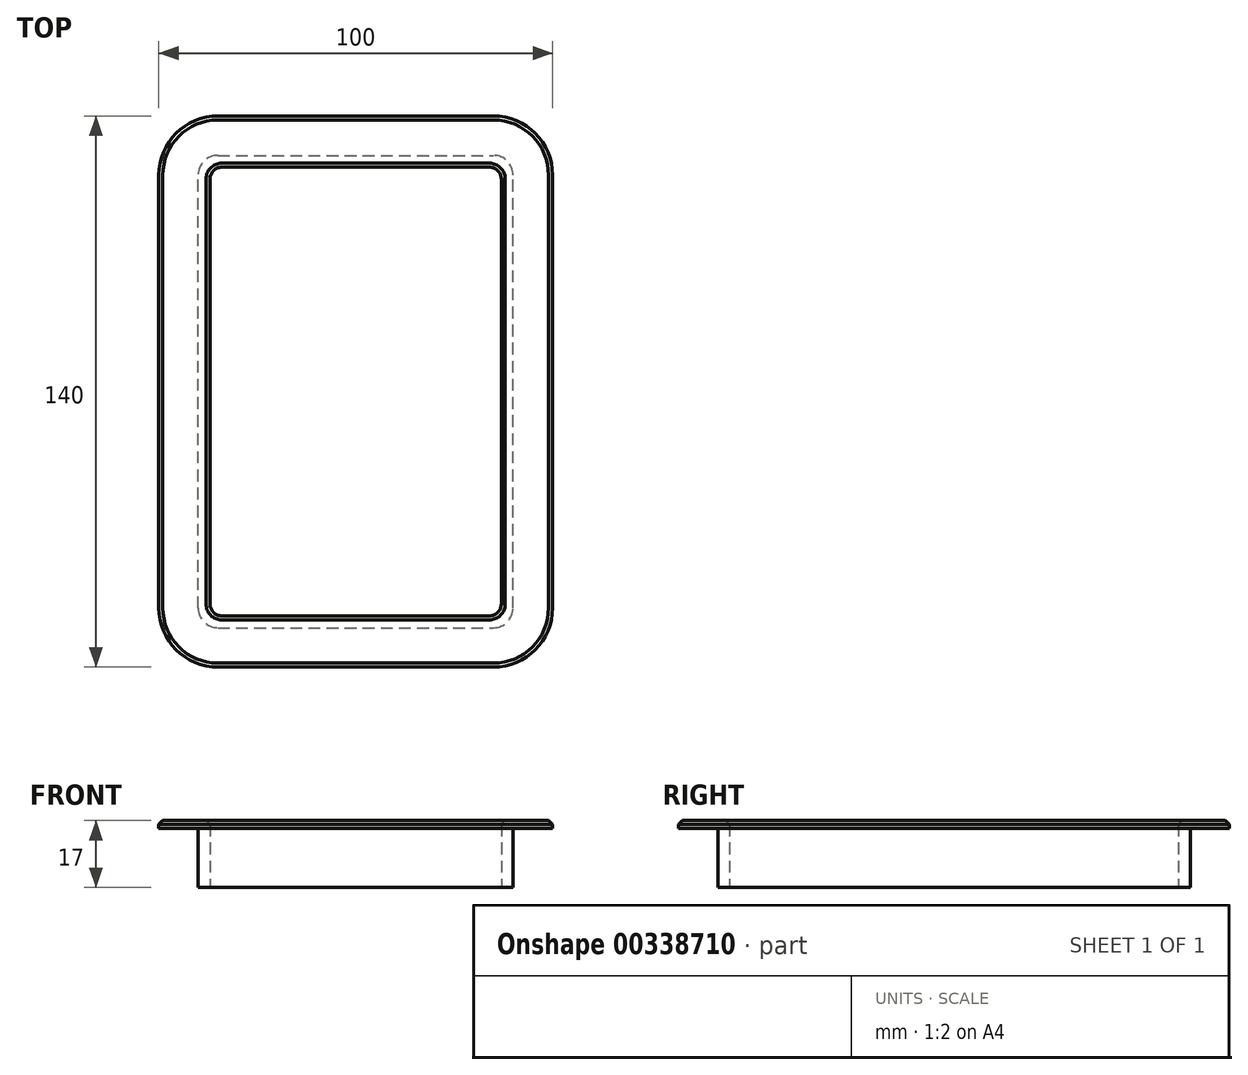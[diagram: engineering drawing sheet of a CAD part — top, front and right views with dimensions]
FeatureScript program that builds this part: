
annotation { "Feature Type Name" : "Feature", "Feature Type Description" : "" }
export const myFeature = defineFeature(function(context is Context, id is Id, definition is map)
    precondition{}
    {
        {
            var Q0;
            Q0=qCreatedBy(makeId("Top.planeOp"),FACE);
            var sketch = newSketch(context, id + "F0", { "sketchPlane" : qUnion([Q0])});
            skLineSegment(sketch, "E0.bottom", {"start": v(5, 0) * mm, "end": v(75, 0) * mm});
            skLineSegment(sketch, "E0.top", {"start": v(5, 120) * mm, "end": v(75, 120) * mm});
            skLineSegment(sketch, "E0.left", {"start": v(0, 5) * mm, "end": v(0, 115) * mm});
            skLineSegment(sketch, "E0.right", {"start": v(80, 5) * mm, "end": v(80, 115) * mm});
            skPoint(sketch, "E1.visualSharp", {"position": v(0, 120) * mm});
            skArc(sketch, "E1.filletArc", {"start": v(5, 120) * mm, "mid": v(1.46, 118.54) * mm, "end": v(0, 115) * mm});
            skPoint(sketch, "E2.visualSharp", {"position": v(80, 120) * mm});
            skArc(sketch, "E2.filletArc", {"start": v(80, 115) * mm, "mid": v(78.54, 118.54) * mm, "end": v(75, 120) * mm});
            skPoint(sketch, "E3.visualSharp", {"position": v(80, 0) * mm});
            skArc(sketch, "E3.filletArc", {"start": v(75, 0) * mm, "mid": v(78.54, 1.46) * mm, "end": v(80, 5) * mm});
            skPoint(sketch, "E4.visualSharp", {"position": v(0, 0) * mm});
            skArc(sketch, "E4.filletArc", {"start": v(0, 5) * mm, "mid": v(1.46, 1.46) * mm, "end": v(5, 0) * mm});
            skLineSegment(sketch, "E5.0", {"start": v(77, 6) * mm, "end": v(77, 114) * mm});
            skLineSegment(sketch, "E5.1", {"start": v(6, 3) * mm, "end": v(74, 3) * mm});
            skLineSegment(sketch, "E5.2", {"start": v(3, 6) * mm, "end": v(3, 114) * mm});
            skLineSegment(sketch, "E5.3", {"start": v(6, 117) * mm, "end": v(74, 117) * mm});
            skPoint(sketch, "E6.visualSharp", {"position": v(77, 117) * mm});
            skArc(sketch, "E6.filletArc", {"start": v(77, 114) * mm, "mid": v(76.12, 116.12) * mm, "end": v(74, 117) * mm});
            skPoint(sketch, "E7.visualSharp", {"position": v(77, 3) * mm});
            skArc(sketch, "E7.filletArc", {"start": v(74, 3) * mm, "mid": v(76.12, 3.88) * mm, "end": v(77, 6) * mm});
            skPoint(sketch, "E8.visualSharp", {"position": v(3, 3) * mm});
            skArc(sketch, "E8.filletArc", {"start": v(3, 6) * mm, "mid": v(3.88, 3.88) * mm, "end": v(6, 3) * mm});
            skPoint(sketch, "E9.visualSharp", {"position": v(3, 117) * mm});
            skArc(sketch, "E9.filletArc", {"start": v(6, 117) * mm, "mid": v(3.88, 116.12) * mm, "end": v(3, 114) * mm});
            skArc(sketch, "E10.0", {"start": v(75, -10) * mm, "mid": v(85.6, -5.6) * mm, "end": v(90, 5) * mm});
            skLineSegment(sketch, "E10.1", {"start": v(5, -10) * mm, "end": v(75, -10) * mm});
            skLineSegment(sketch, "E10.2", {"start": v(90, 5) * mm, "end": v(90, 115) * mm});
            skArc(sketch, "E10.3", {"start": v(-10, 5) * mm, "mid": v(-5.6, -5.6) * mm, "end": v(5, -10) * mm});
            skArc(sketch, "E10.4", {"start": v(90, 115) * mm, "mid": v(85.6, 125.6) * mm, "end": v(75, 130) * mm});
            skLineSegment(sketch, "E10.5", {"start": v(5, 130) * mm, "end": v(75, 130) * mm});
            skArc(sketch, "E10.6", {"start": v(5, 130) * mm, "mid": v(-5.6, 125.6) * mm, "end": v(-10, 115) * mm});
            skLineSegment(sketch, "E10.7", {"start": v(-10, 5) * mm, "end": v(-10, 115) * mm});
            skSolve(sketch);
        }
        {
            var Q0;
            Q0=makeQuery(id+"F0.imprint","IMPRINT",FACE,{"disambiguationData":[TD([[makeQuery(id+"F0.imprint","IMPRINT",EDGE,{"derivedFrom":sQuery(id+"F0.wireOp",EDGE,"E0.bottom")}),-1.0]])]});
            var Q1;
            Q1=makeQuery(id+"F0.imprint","IMPRINT",FACE,{"disambiguationData":[TD([[makeQuery(id+"F0.imprint","IMPRINT",EDGE,{"derivedFrom":sQuery(id+"F0.wireOp",EDGE,"E0.bottom")}),1.0]])]});
            extrude(context, id + "F1", {"entities" : qUnion([Q0, Q1]), "depth" : 2 * mm});
        }
        {
            var Q0;
            Q0=makeQuery(id+"F0.imprint","IMPRINT",FACE,{"disambiguationData":[TD([[makeQuery(id+"F0.imprint","IMPRINT",EDGE,{"derivedFrom":sQuery(id+"F0.wireOp",EDGE,"E0.bottom")}),1.0]])]});
            extrude(context, id + "F2", {"entities" : qUnion([Q0]), "operationType" : NewBodyOperationType.ADD, "oppositeDirection" : true, "depth" : 15 * mm});
        }
        {
            var Q0;
            Q0=makeQuery(id+"F1.opExtrude","CAP_EDGE",EDGE,{"disambiguationData":[OSD([sQuery(id+"F0.wireOp",EDGE,"E5.0")])],"isStart":false});
            var Q1;
            Q1=makeQuery(id+"F1.opExtrude","CAP_EDGE",EDGE,{"disambiguationData":[OSD([sQuery(id+"F0.wireOp",EDGE,"E6.filletArc")])],"isStart":false});
            var Q2;
            Q2=makeQuery(id+"F1.opExtrude","CAP_EDGE",EDGE,{"disambiguationData":[OSD([sQuery(id+"F0.wireOp",EDGE,"E5.3")])],"isStart":false});
            var Q3;
            Q3=makeQuery(id+"F1.opExtrude","CAP_EDGE",EDGE,{"disambiguationData":[OSD([sQuery(id+"F0.wireOp",EDGE,"E9.filletArc")])],"isStart":false});
            var Q4;
            Q4=makeQuery(id+"F1.opExtrude","CAP_EDGE",EDGE,{"disambiguationData":[OSD([sQuery(id+"F0.wireOp",EDGE,"E5.2")])],"isStart":false});
            var Q5;
            Q5=makeQuery(id+"F1.opExtrude","CAP_EDGE",EDGE,{"disambiguationData":[OSD([sQuery(id+"F0.wireOp",EDGE,"E5.1")])],"isStart":false});
            var Q6;
            Q6=makeQuery(id+"F1.opExtrude","CAP_EDGE",EDGE,{"disambiguationData":[OSD([sQuery(id+"F0.wireOp",EDGE,"E7.filletArc")])],"isStart":false});
            var Q7;
            Q7=makeQuery(id+"F1.opExtrude","CAP_EDGE",EDGE,{"disambiguationData":[OSD([sQuery(id+"F0.wireOp",EDGE,"E8.filletArc")])],"isStart":false});
            var Q8;
            Q8=makeQuery(id+"F1.opExtrude","CAP_EDGE",EDGE,{"disambiguationData":[OSD([sQuery(id+"F0.wireOp",EDGE,"E10.3")])],"isStart":false});
            var Q9;
            Q9=makeQuery(id+"F1.opExtrude","CAP_EDGE",EDGE,{"disambiguationData":[OSD([sQuery(id+"F0.wireOp",EDGE,"E10.1")])],"isStart":false});
            var Q10;
            Q10=makeQuery(id+"F1.opExtrude","CAP_EDGE",EDGE,{"disambiguationData":[OSD([sQuery(id+"F0.wireOp",EDGE,"E10.0")])],"isStart":false});
            var Q11;
            Q11=makeQuery(id+"F1.opExtrude","CAP_EDGE",EDGE,{"disambiguationData":[OSD([sQuery(id+"F0.wireOp",EDGE,"E10.2")])],"isStart":false});
            var Q12;
            Q12=makeQuery(id+"F1.opExtrude","CAP_EDGE",EDGE,{"disambiguationData":[OSD([sQuery(id+"F0.wireOp",EDGE,"E10.7")])],"isStart":false});
            var Q13;
            Q13=makeQuery(id+"F1.opExtrude","CAP_EDGE",EDGE,{"disambiguationData":[OSD([sQuery(id+"F0.wireOp",EDGE,"E10.5")])],"isStart":false});
            var Q14;
            Q14=makeQuery(id+"F1.opExtrude","CAP_EDGE",EDGE,{"disambiguationData":[OSD([sQuery(id+"F0.wireOp",EDGE,"E10.6")])],"isStart":false});
            var Q15;
            Q15=makeQuery(id+"F1.opExtrude","CAP_EDGE",EDGE,{"disambiguationData":[OSD([sQuery(id+"F0.wireOp",EDGE,"E10.4")])],"isStart":false});
            chamfer(context, id + "F3", {"entities" : qUnion([Q0, Q1, Q2, Q3, Q4, Q5, Q6, Q7, Q8, Q9, Q10, Q11, Q12, Q13, Q14, Q15]), "width" : 1 * mm, "tangentPropagation" : true});
        }
    });
